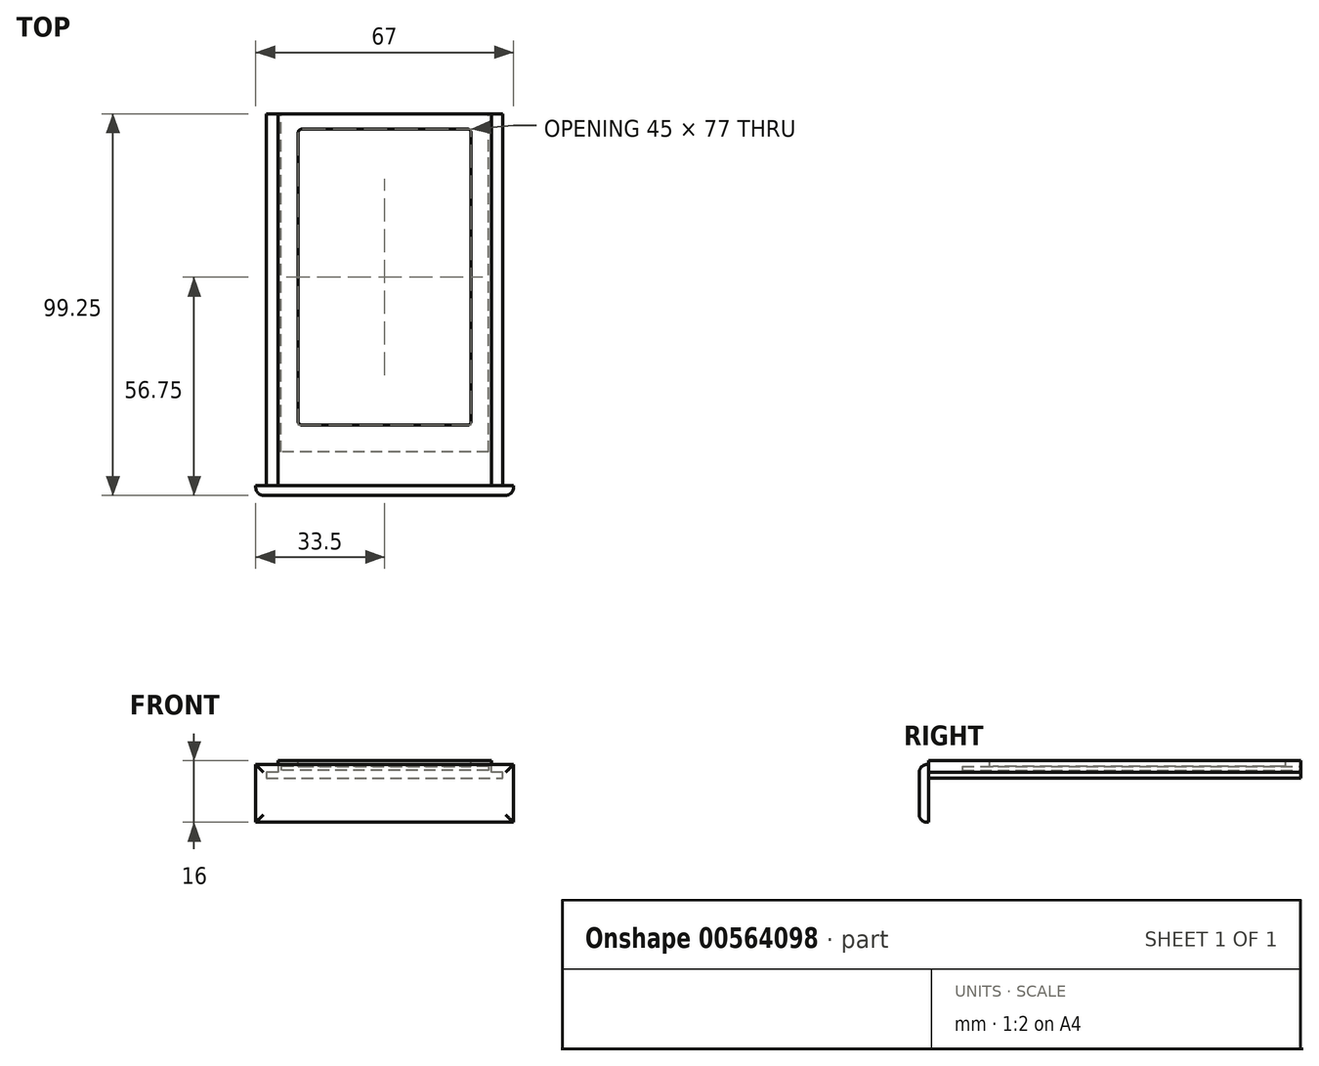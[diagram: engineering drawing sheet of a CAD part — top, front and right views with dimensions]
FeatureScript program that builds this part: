
annotation { "Feature Type Name" : "Feature", "Feature Type Description" : "" }
export const myFeature = defineFeature(function(context is Context, id is Id, definition is map)
    precondition{}
    {
        {
            var Q0;
            Q0=qCreatedBy(makeId("Front.planeOp"),FACE);
            var sketch = newSketch(context, id + "F0", { "sketchPlane" : qUnion([Q0])});
            skLineSegment(sketch, "E0", {"start": v(-27.75, -3) * mm, "end": v(-30.75, -3) * mm});
            skLineSegment(sketch, "E1", {"start": v(-30.75, -3) * mm, "end": v(-30.75, -4.5) * mm});
            skLineSegment(sketch, "E2", {"start": v(-30.75, -4.5) * mm, "end": v(30.75, -4.5) * mm});
            skLineSegment(sketch, "E3", {"start": v(30.75, -4.5) * mm, "end": v(30.75, -3) * mm});
            skLineSegment(sketch, "E4", {"start": v(30.75, -3) * mm, "end": v(27.75, -3) * mm});
            skLineSegment(sketch, "E5", {"start": v(27.75, -3) * mm, "end": v(27.75, 0) * mm});
            skLineSegment(sketch, "E6", {"start": v(27.75, 0) * mm, "end": v(-27.75, 0) * mm});
            skLineSegment(sketch, "E7", {"start": v(-27.75, 0) * mm, "end": v(-27.75, -3) * mm});
            skSolve(sketch);
        }
        {
            var Q0;
            Q0=makeQuery(id+"F0.imprint","IMPRINT",FACE,{"disambiguationData":[TD([[makeQuery(id+"F0.imprint","IMPRINT",EDGE,{"derivedFrom":sQuery(id+"F0.wireOp",EDGE,"E0")}),1.0]])]});
            extrude(context, id + "F1", {"entities" : qUnion([Q0]), "depth" : 96.75 * mm, "offsetDistance" : 25 * mm});
        }
        {
            var Q0;
            Q0=makeQuery(id+"F1.opExtrude","CAP_FACE",FACE,{"disambiguationData":[OSD([sQuery(id+"F0.wireOp",EDGE,"E0"),sQuery(id+"F0.wireOp",EDGE,"E1"),sQuery(id+"F0.wireOp",EDGE,"E2"),sQuery(id+"F0.wireOp",EDGE,"E3"),sQuery(id+"F0.wireOp",EDGE,"E4"),sQuery(id+"F0.wireOp",EDGE,"E5"),sQuery(id+"F0.wireOp",EDGE,"E6"),sQuery(id+"F0.wireOp",EDGE,"E7")])],"isStart":false});
            var sketch = newSketch(context, id + "F2", { "sketchPlane" : qUnion([Q0])});
            skLineSegment(sketch, "E8.bottom", {"start": v(-33.5, -1) * mm, "end": v(33.5, -1) * mm});
            skLineSegment(sketch, "E8.top", {"start": v(-33.5, -16) * mm, "end": v(33.5, -16) * mm});
            skLineSegment(sketch, "E8.left", {"start": v(-33.5, -1) * mm, "end": v(-33.5, -16) * mm});
            skLineSegment(sketch, "E8.right", {"start": v(33.5, -1) * mm, "end": v(33.5, -16) * mm});
            skSolve(sketch);
        }
        {
            var Q0;
            Q0 = qSketchRegion(id + "F2", true);
            extrude(context, id + "F3", {"entities" : qUnion([Q0]), "operationType" : NewBodyOperationType.ADD, "depth" : 2.5 * mm, "offsetDistance" : 25 * mm});
        }
        {
            var Q0;
            Q0=makeQuery(id+"F1.opExtrude","CAP_FACE",FACE,{"disambiguationData":[OSD([sQuery(id+"F0.wireOp",EDGE,"E0"),sQuery(id+"F0.wireOp",EDGE,"E1"),sQuery(id+"F0.wireOp",EDGE,"E2"),sQuery(id+"F0.wireOp",EDGE,"E3"),sQuery(id+"F0.wireOp",EDGE,"E4"),sQuery(id+"F0.wireOp",EDGE,"E5"),sQuery(id+"F0.wireOp",EDGE,"E6"),sQuery(id+"F0.wireOp",EDGE,"E7")])],"isStart":true});
            var sketch = newSketch(context, id + "F4", { "sketchPlane" : qUnion([Q0])});
            skLineSegment(sketch, "E9.bottom", {"start": v(-27, -1.5) * mm, "end": v(27, -1.5) * mm});
            skLineSegment(sketch, "E9.top", {"start": v(-27, -2.5) * mm, "end": v(27, -2.5) * mm});
            skLineSegment(sketch, "E9.left", {"start": v(-27, -1.5) * mm, "end": v(-27, -2.5) * mm});
            skLineSegment(sketch, "E9.right", {"start": v(27, -1.5) * mm, "end": v(27, -2.5) * mm});
            skSolve(sketch);
        }
        {
            var Q0;
            Q0=makeQuery(id+"F4.imprint","IMPRINT",FACE,{"disambiguationData":[TD([[makeQuery(id+"F4.imprint","IMPRINT",EDGE,{"derivedFrom":sQuery(id+"F4.wireOp",EDGE,"E9.bottom")}),-1.0]])]});
            extrude(context, id + "F5", {"entities" : qUnion([Q0]), "operationType" : NewBodyOperationType.REMOVE, "oppositeDirection" : true, "depth" : 88 * mm, "offsetDistance" : 25 * mm});
        }
        {
            var Q0;
            Q0=makeQuery(id+"F1.opExtrude","SWEPT_FACE",FACE,{"disambiguationData":[OSD([sQuery(id+"F0.wireOp",EDGE,"E6")])]});
            var sketch = newSketch(context, id + "F6", { "sketchPlane" : qUnion([Q0])});
            skLineSegment(sketch, "E10.bottom", {"start": v(-22.5, -4) * mm, "end": v(22.5, -4) * mm});
            skLineSegment(sketch, "E10.top", {"start": v(-22.5, -81) * mm, "end": v(22.5, -81) * mm});
            skLineSegment(sketch, "E10.left", {"start": v(-22.5, -4) * mm, "end": v(-22.5, -81) * mm});
            skLineSegment(sketch, "E10.right", {"start": v(22.5, -4) * mm, "end": v(22.5, -81) * mm});
            skSolve(sketch);
        }
        {
            var Q0;
            Q0=makeQuery(id+"F6.imprint","IMPRINT",FACE,{"disambiguationData":[TD([[makeQuery(id+"F6.imprint","IMPRINT",EDGE,{"derivedFrom":sQuery(id+"F6.wireOp",EDGE,"E10.bottom")}),-1.0]])]});
            extrude(context, id + "F7", {"entities" : qUnion([Q0]), "operationType" : NewBodyOperationType.REMOVE, "endBound" : BoundingType.UP_TO_NEXT, "oppositeDirection" : true, "depth" : 25 * mm, "offsetDistance" : 25 * mm});
        }
        {
            var Q0;
            Q0=makeQuery(id+"F7.boolean.opBoolean","COPY",EDGE,{"derivedFrom":makeQuery(id+"F7.opExtrude","SWEPT_EDGE",EDGE,{"disambiguationData":[OSD([sQuery(id+"F6.wireOp",EDGE,"E10.top"),sQuery(id+"F6.wireOp",EDGE,"E10.left")])]})});
            var Q1;
            Q1=makeQuery(id+"F7.boolean.opBoolean","COPY",EDGE,{"derivedFrom":makeQuery(id+"F7.opExtrude","SWEPT_EDGE",EDGE,{"disambiguationData":[OSD([sQuery(id+"F6.wireOp",EDGE,"E10.bottom"),sQuery(id+"F6.wireOp",EDGE,"E10.left")])]})});
            var Q2;
            Q2=makeQuery(id+"F7.boolean.opBoolean","COPY",EDGE,{"derivedFrom":makeQuery(id+"F7.opExtrude","SWEPT_EDGE",EDGE,{"disambiguationData":[OSD([sQuery(id+"F6.wireOp",EDGE,"E10.bottom"),sQuery(id+"F6.wireOp",EDGE,"E10.right")])]})});
            var Q3;
            Q3=makeQuery(id+"F7.boolean.opBoolean","COPY",EDGE,{"derivedFrom":makeQuery(id+"F7.opExtrude","SWEPT_EDGE",EDGE,{"disambiguationData":[OSD([sQuery(id+"F6.wireOp",EDGE,"E10.top"),sQuery(id+"F6.wireOp",EDGE,"E10.right")])]})});
            fillet(context, id + "F8", {"entities" : qUnion([Q0, Q1, Q2, Q3]), "radius" : 1 * mm, "tangentPropagation" : true, "allowEdgeOverflow" : false});
        }
        {
            var Q0;
            Q0=makeQuery(id+"F3.opExtrude","CAP_EDGE",EDGE,{"disambiguationData":[OSD([sQuery(id+"F2.wireOp",EDGE,"E8.top")])],"isStart":false});
            var Q1;
            Q1=makeQuery(id+"F3.opExtrude","CAP_EDGE",EDGE,{"disambiguationData":[OSD([sQuery(id+"F2.wireOp",EDGE,"E8.bottom")])],"isStart":false});
            var Q2;
            Q2=makeQuery(id+"F3.opExtrude","CAP_EDGE",EDGE,{"disambiguationData":[OSD([sQuery(id+"F2.wireOp",EDGE,"E8.right")])],"isStart":false});
            var Q3;
            Q3=makeQuery(id+"F3.opExtrude","CAP_EDGE",EDGE,{"disambiguationData":[OSD([sQuery(id+"F2.wireOp",EDGE,"E8.left")])],"isStart":false});
            fillet(context, id + "F9", {"entities" : qUnion([Q0, Q1, Q2, Q3]), "radius" : 2 * mm, "tangentPropagation" : true, "allowEdgeOverflow" : false});
        }
    });
